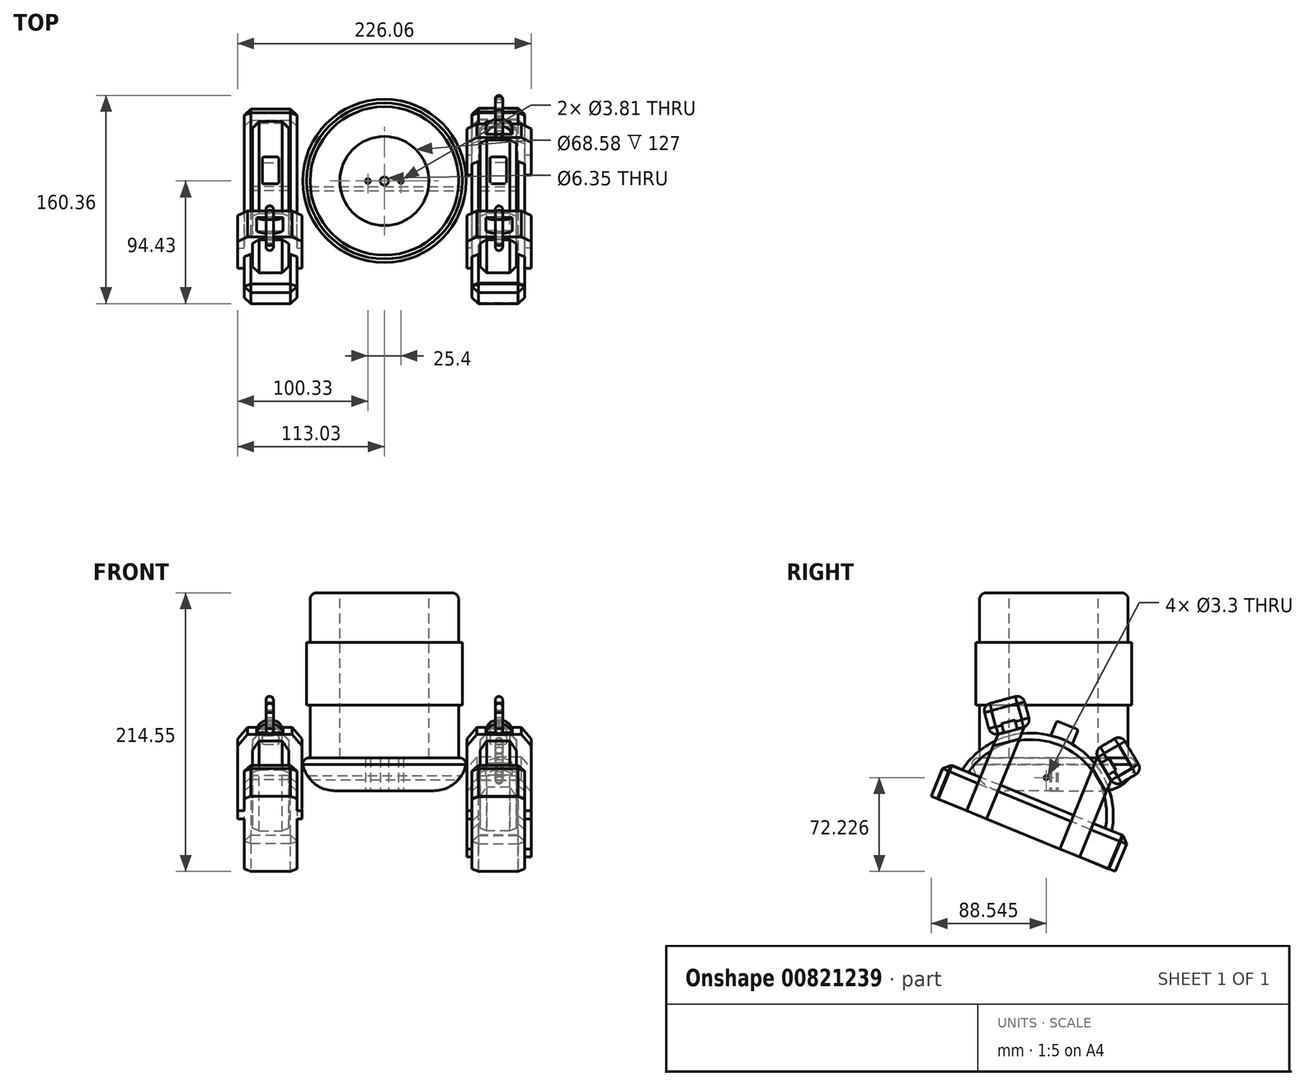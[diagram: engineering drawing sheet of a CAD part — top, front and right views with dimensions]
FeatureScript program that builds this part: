
annotation { "Feature Type Name" : "Feature", "Feature Type Description" : "" }
export const myFeature = defineFeature(function(context is Context, id is Id, definition is map)
    precondition{}
    {
        {
            assignVariable(context, id + "F0", {"name" : "Length", "anyValue" : 127 * mm});
        }
        {
            var Q0;
            Q0=qCreatedBy(makeId("Top.planeOp"),FACE);
            var sketch = newSketch(context, id + "F1", { "sketchPlane" : qUnion([Q0])});
            skCircle(sketch, "E0", {"center": v(0, 0) * mm, "radius": 57.15 * mm});
            skSolve(sketch);
        }
        {
            var Q0;
            Q0 = qSketchRegion(id + "F1", true);
            extrude(context, id + "F2", {"entities" : qUnion([Q0]), "depth" : getVariable(context, 'Length'), "offsetDistance" : 25.4 * mm});
        }
        {
            var Q0;
            Q0=makeQuery(id+"F2.opExtrude","CAP_FACE",FACE,{"disambiguationData":[OSD([sQuery(id+"F1.wireOp",EDGE,"E0")])],"isStart":false});
            var sketch = newSketch(context, id + "F3", { "sketchPlane" : qUnion([Q0])});
            skCircle(sketch, "E1", {"center": v(0, 0) * mm, "radius": 34.3 * mm});
            skSolve(sketch);
        }
        {
            var Q0;
            Q0=makeQuery(id+"F7.boolean.opBoolean","COPY",EDGE,{"derivedFrom":makeQuery(id+"F7.opExtrude","CAP_EDGE",EDGE,{"disambiguationData":[OSD([sQuery(id+"F3.wireOp",EDGE,"E1")])],"isStart":true})});
            var Q1;
            Q1=makeQuery(id+"F2.opExtrude","CAP_EDGE",EDGE,{"disambiguationData":[OSD([sQuery(id+"F1.wireOp",EDGE,"E0")])],"isStart":false});
            fillet(context, id + "F4", {"entities" : qUnion([Q0, Q1]), "radius" : 5.08 * mm, "tangentPropagation" : true, "allowEdgeOverflow" : false});
        }
        {
            var Q0;
            Q0=qCreatedBy(makeId("Top.planeOp"),FACE);
            var sketch = newSketch(context, id + "F5", { "sketchPlane" : qUnion([Q0])});
            skCircle(sketch, "E2", {"center": v(0, 0) * mm, "radius": 60 * mm});
            skSolve(sketch);
        }
        {
            var Q0;
            Q0=makeQuery(id+"F5.imprint","IMPRINT",FACE,{"disambiguationData":[TD([[makeQuery(id+"F5.imprint","IMPRINT",EDGE,{"derivedFrom":sQuery(id+"F5.wireOp",EDGE,"E2")}),1.0]])]});
            extrude(context, id + "F6", {"entities" : qUnion([Q0]), "operationType" : NewBodyOperationType.ADD, "depth" : 88.9 * mm, "offsetDistance" : 25.4 * mm, "hasSecondDirection" : true, "secondDirectionOppositeDirection" : false, "secondDirectionDepth" : 40.64 * mm});
        }
        {
            var Q0;
            Q0=makeQuery(id+"F3.imprint","IMPRINT",FACE,{"disambiguationData":[TD([[makeQuery(id+"F3.imprint","IMPRINT",EDGE,{"derivedFrom":sQuery(id+"F3.wireOp",EDGE,"E1")}),1.0]])]});
            extrude(context, id + "F7", {"entities" : qUnion([Q0]), "operationType" : NewBodyOperationType.REMOVE, "oppositeDirection" : true, "depth" : getVariable(context, 'Length'), "offsetDistance" : 25.4 * mm});
        }
        {
            var Q0;
            Q0=qCreatedBy(makeId("Top.planeOp"),FACE);
            var sketch = newSketch(context, id + "F8", { "sketchPlane" : qUnion([Q0])});
            skCircle(sketch, "E3", {"center": v(0, 0) * mm, "radius": 62.87 * mm});
            skSolve(sketch);
        }
        {
            var Q0;
            Q0 = qSketchRegion(id + "F8", true);
            extrude(context, id + "F9", {"entities" : qUnion([Q0]), "operationType" : NewBodyOperationType.ADD, "oppositeDirection" : true, "depth" : .1 * getVariable(context, 'Length'), "offsetDistance" : 25.4 * mm});
        }
        {
            var Q0;
            Q0=makeQuery(id+"F9.opExtrude","CAP_EDGE",EDGE,{"disambiguationData":[OSD([sQuery(id+"F8.wireOp",EDGE,"E3")])],"isStart":true});
            fillet(context, id + "F10", {"entities" : qUnion([Q0]), "radius" : 5.08 * mm, "tangentPropagation" : true, "allowEdgeOverflow" : false});
        }
        {
            var Q0;
            Q0=makeQuery(id+"F9.opExtrude","CAP_FACE",FACE,{"disambiguationData":[OSD([sQuery(id+"F8.wireOp",EDGE,"E3")])],"isStart":false});
            var sketch = newSketch(context, id + "F11", { "sketchPlane" : qUnion([Q0])});
            skCircle(sketch, "E4", {"center": v(0, 0) * mm, "radius": 62.87 * mm});
            skSolve(sketch);
        }
        {
            var Q0;
            Q0 = qSketchRegion(id + "F11", true);
            extrude(context, id + "F12", {"entities" : qUnion([Q0]), "operationType" : NewBodyOperationType.ADD, "depth" : .1 * getVariable(context, 'Length'), "offsetDistance" : 25.4 * mm});
        }
        {
            var Q0;
            Q0=makeQuery(id+"F12.opExtrude","CAP_EDGE",EDGE,{"disambiguationData":[OSD([sQuery(id+"F11.wireOp",EDGE,"E4")])],"isStart":false});
            fillet(context, id + "F13", {"entities" : qUnion([Q0]), "radius" : 25.4 * mm, "tangentPropagation" : true, "allowEdgeOverflow" : false});
        }
        {
            var Q0;
            Q0=makeQuery(id+"F12.opExtrude","CAP_FACE",FACE,{"disambiguationData":[OSD([sQuery(id+"F11.wireOp",EDGE,"E4")])],"isStart":false});
            var sketch = newSketch(context, id + "F14", { "sketchPlane" : qUnion([Q0])});
            skLineSegment(sketch, "E5", {"start": v(0, 0) * mm, "end": v(-12.7, 0) * mm, "construction": true});
            skLineSegment(sketch, "E6", {"start": v(0, 0) * mm, "end": v(12.7, 0) * mm, "construction": true});
            skCircle(sketch, "E7", {"center": v(-12.7, 0) * mm, "radius": 1.9 * mm});
            skCircle(sketch, "E8", {"center": v(12.7, 0) * mm, "radius": 1.9 * mm});
            skCircle(sketch, "E9", {"center": v(0, 0) * mm, "radius": 3.18 * mm});
            skSolve(sketch);
        }
        {
            var Q0;
            Q0=makeQuery(id+"F9.boolean.opBoolean","SPLIT",FACE,{"disambiguationData":[TD([makeQuery(id+"F7.boolean.opBoolean","COPY",FACE,{"derivedFrom":makeQuery(id+"F7.opExtrude","SWEPT_FACE",FACE,{"disambiguationData":[OSD([sQuery(id+"F3.wireOp",EDGE,"E1")])]})})])],"derivedFrom":makeQuery(id+"F9.opExtrude","CAP_FACE",FACE,{"disambiguationData":[OSD([sQuery(id+"F8.wireOp",EDGE,"E3")])],"isStart":true})});
            var sketch = newSketch(context, id + "F15", { "sketchPlane" : qUnion([Q0])});
            skCircle(sketch, "E10", {"center": v(0, 0) * mm, "radius": 29.15 * mm});
            skSolve(sketch);
        }
        {
            var Q0;
            Q0=makeQuery(id+"F14.imprint","IMPRINT",FACE,{"disambiguationData":[TD([[makeQuery(id+"F14.imprint","IMPRINT",EDGE,{"derivedFrom":sQuery(id+"F14.wireOp",EDGE,"E7")}),1.0]])]});
            var Q1;
            Q1=makeQuery(id+"F14.imprint","IMPRINT",FACE,{"disambiguationData":[TD([[makeQuery(id+"F14.imprint","IMPRINT",EDGE,{"derivedFrom":sQuery(id+"F14.wireOp",EDGE,"E8")}),1.0]])]});
            var Q2;
            Q2=makeQuery(id+"F14.imprint","IMPRINT",FACE,{"disambiguationData":[TD([[makeQuery(id+"F14.imprint","IMPRINT",EDGE,{"derivedFrom":sQuery(id+"F14.wireOp",EDGE,"E9")}),1.0]])]});
            var Q3;
            Q3=sQuery(id+"F14.wireOp",EDGE,"E7");
            var Q4;
            Q4=sQuery(id+"F14.wireOp",EDGE,"E8");
            var Q5;
            Q5=sQuery(id+"F15.wireOp",EDGE,"E10");
            extrude(context, id + "F16", {"entities" : qUnion([Q0, Q1, Q2]), "operationType" : NewBodyOperationType.REMOVE, "surfaceEntities" : qUnion([Q3, Q4, Q5]), "oppositeDirection" : true, "depth" : 61.2 * mm, "offsetDistance" : 25.4 * mm});
        }
        {
            var Q0;
            Q0=qCreatedBy(makeId("Right.planeOp"),FACE);
            var sketch = newSketch(context, id + "F17", { "sketchPlane" : qUnion([Q0])});
            skLineSegment(sketch, "E11", {"start": v(0, 0) * mm, "end": v(0, -44.45) * mm, "construction": true});
            skLineSegment(sketch, "E12", {"start": v(0, -44.45) * mm, "end": v(-17.78, -44.45) * mm, "construction": true});
            skCircle(sketch, "E13", {"center": v(-17.78, -44.45) * mm, "radius": 63.5 * mm});
            skLineSegment(sketch, "E14", {"start": v(-77.05, -21.67) * mm, "end": v(40.5, -69.68) * mm});
            skSolve(sketch);
        }
        {
            var Q0;
            {var subQ0=sQuery(id+"F17.wireOp",EDGE,"E14");Q0=makeQuery(id+"F17.imprint","IMPRINT",FACE,{"disambiguationData":[TD([[makeQuery(id+"F17.imprint","IMPRINT",EDGE,{"derivedFrom":subQ0}),1.0]])]});}
            extrude(context, id + "F18", {"entities" : qUnion([Q0]), "depth" : 101.6 * mm, "offsetDistance" : 25.4 * mm, "hasSecondDirection" : true, "secondDirectionOppositeDirection" : false, "secondDirectionDepth" : 73.66 * mm});
        }
        {
            var Q0;
            Q0=makeQuery(id+"F18.opExtrude","CAP_EDGE",EDGE,{"disambiguationData":[OSD([sQuery(id+"F17.wireOp",EDGE,"E13")])],"isStart":true});
            cPoint(context, id + "F19", {"entities" : qUnion([Q0]), "parameter" : 0.5});
        }
        {
            var Q0;
            Q0=makeQuery(id+"F18.opExtrude","CAP_EDGE",EDGE,{"disambiguationData":[OSD([sQuery(id+"F17.wireOp",EDGE,"E13")])],"isStart":false});
            var Q1;
            Q1 = qCreatedBy(id + "F19" ,VERTEX);
            cPlane(context, id + "F20", {"entities" : qUnion([Q0, Q1]), "cplaneType" : CPlaneType.CURVE_POINT, "offset" : 25.4 * mm, "width" : 152.4 * mm, "height" : 152.4 * mm});
        }
        {
            var Q0;
            Q0=makeQuery(id+"F18.opExtrude","SWEPT_FACE",FACE,{"disambiguationData":[OSD([sQuery(id+"F17.wireOp",EDGE,"E14")])]});
            var sketch = newSketch(context, id + "F21", { "sketchPlane" : qUnion([Q0])});
            skLineSegment(sketch, "E15.bottom", {"start": v(107.95, 76.2) * mm, "end": v(67.31, 76.2) * mm});
            skLineSegment(sketch, "E15.top", {"start": v(107.95, -76.2) * mm, "end": v(67.31, -76.2) * mm});
            skLineSegment(sketch, "E15.left", {"start": v(107.95, 76.2) * mm, "end": v(107.95, -76.2) * mm});
            skLineSegment(sketch, "E15.right", {"start": v(67.31, 76.2) * mm, "end": v(67.31, -76.2) * mm});
            skPoint(sketch, "E15.middle", {"position": v(87.63, 0) * mm});
            skPoint(sketch, "E15.middle.positionSnap0", {"position": v(87.63, 63.14) * mm});
            skPoint(sketch, "E15.centerSnap0", {"position": v(87.63, 63.14) * mm});
            skSolve(sketch);
        }
        {
            var Q0;
            Q0=makeQuery(id+"F21.imprint","IMPRINT",FACE,{"disambiguationData":[TD([[makeQuery(id+"F21.imprint","IMPRINT",EDGE,{"derivedFrom":sQuery(id+"F21.wireOp",EDGE,"E15.bottom")}),1.0]])]});
            var Q1;
            {var subQ0=sQuery(id+"F17.wireOp",EDGE,"E14");Q1=makeQuery(id+"F21.imprint","IMPRINT",FACE,{"disambiguationData":[TD([[makeQuery(id+"F21.imprint","IMPRINT",EDGE,{"derivedFrom":makeQuery(id+"F18.opExtrude","CAP_EDGE",EDGE,{"disambiguationData":[OSD([subQ0])],"isStart":true})}),1.0]])]});}
            extrude(context, id + "F22", {"entities" : qUnion([Q0, Q1]), "operationType" : NewBodyOperationType.ADD, "depth" : 13.97 * mm, "offsetDistance" : 25.4 * mm, "hasSecondDirection" : true, "secondDirectionOppositeDirection" : true, "secondDirectionDepth" : 13.97 * mm});
        }
        {
            var Q0;
            Q0=makeQuery(id+"F22.opExtrude","CAP_EDGE",EDGE,{"disambiguationData":[OSD([sQuery(id+"F21.wireOp",EDGE,"E15.bottom")])],"isStart":true});
            var Q1;
            Q1=makeQuery(id+"F22.opExtrude","CAP_EDGE",EDGE,{"disambiguationData":[OSD([sQuery(id+"F21.wireOp",EDGE,"E15.left")])],"isStart":true});
            var Q2;
            Q2=makeQuery(id+"F22.opExtrude","CAP_EDGE",EDGE,{"disambiguationData":[OSD([sQuery(id+"F21.wireOp",EDGE,"E15.right")])],"isStart":true});
            var Q3;
            Q3=makeQuery(id+"F22.opExtrude","SWEPT_EDGE",EDGE,{"disambiguationData":[OSD([sQuery(id+"F21.wireOp",EDGE,"E15.bottom"),sQuery(id+"F21.wireOp",EDGE,"E15.left")])]});
            var Q4;
            Q4=makeQuery(id+"F22.opExtrude","SWEPT_EDGE",EDGE,{"disambiguationData":[OSD([sQuery(id+"F21.wireOp",EDGE,"E15.bottom"),sQuery(id+"F21.wireOp",EDGE,"E15.right")])]});
            var Q5;
            Q5=makeQuery(id+"F22.opExtrude","SWEPT_EDGE",EDGE,{"disambiguationData":[OSD([sQuery(id+"F21.wireOp",EDGE,"E15.top"),sQuery(id+"F21.wireOp",EDGE,"E15.left")])]});
            var Q6;
            Q6=makeQuery(id+"F22.opExtrude","SWEPT_EDGE",EDGE,{"disambiguationData":[OSD([sQuery(id+"F21.wireOp",EDGE,"E15.top"),sQuery(id+"F21.wireOp",EDGE,"E15.right")])]});
            var Q7;
            Q7=makeQuery(id+"F22.opExtrude","CAP_EDGE",EDGE,{"disambiguationData":[OSD([sQuery(id+"F21.wireOp",EDGE,"E15.top")])],"isStart":true});
            var Q8;
            {var subQ0=sQuery(id+"F17.wireOp",EDGE,"E13");Q8=makeQuery(id+"F22.boolean.opBoolean","SPLIT",EDGE,{"disambiguationData":[topologyDisambiguationEdgeConnected([makeQuery(id+"F18.opExtrude","SWEPT_FACE",FACE,{"disambiguationData":[OSD([subQ0])]}),makeQuery(id+"F18.opExtrude","CAP_FACE",FACE,{"disambiguationData":[OSD([subQ0,sQuery(id+"F17.wireOp",EDGE,"E14")])],"isStart":false})])],"derivedFrom":makeQuery(id+"F18.opExtrude","CAP_EDGE",EDGE,{"disambiguationData":[OSD([subQ0])],"isStart":false})});}
            var Q9;
            {var subQ0=sQuery(id+"F17.wireOp",EDGE,"E13");Q9=makeQuery(id+"F22.boolean.opBoolean","SPLIT",EDGE,{"disambiguationData":[topologyDisambiguationEdgeConnected([makeQuery(id+"F18.opExtrude","SWEPT_FACE",FACE,{"disambiguationData":[OSD([subQ0])]}),makeQuery(id+"F18.opExtrude","CAP_FACE",FACE,{"disambiguationData":[OSD([subQ0,sQuery(id+"F17.wireOp",EDGE,"E14")])],"isStart":true})])],"derivedFrom":makeQuery(id+"F18.opExtrude","CAP_EDGE",EDGE,{"disambiguationData":[OSD([subQ0])],"isStart":true})});}
            chamfer(context, id + "F23", {"entities" : qUnion([Q0, Q1, Q2, Q3, Q4, Q5, Q6, Q7, Q8, Q9]), "width" : 5.08 * mm, "tangentPropagation" : true});
        }
        {
            var Q0;
            Q0=makeQuery(id+"F22.opExtrude","SWEPT_FACE",FACE,{"disambiguationData":[OSD([sQuery(id+"F21.wireOp",EDGE,"E15.left")])]});
            var sketch = newSketch(context, id + "F24", { "sketchPlane" : qUnion([Q0])});
            skLineSegment(sketch, "E16", {"start": v(-51.76, -47.1) * mm, "end": v(-67.05, -40.85) * mm});
            skLineSegment(sketch, "E17", {"start": v(-67.05, -40.85) * mm, "end": v(-43.04, 17.94) * mm});
            skLineSegment(sketch, "E18", {"start": v(-51.76, -47.1) * mm, "end": v(-22.95, 23.45) * mm});
            skLineSegment(sketch, "E19", {"start": v(-22.95, 23.45) * mm, "end": v(-43.04, 17.94) * mm});
            skSolve(sketch);
        }
        {
            var Q0;
            Q0 = qSketchRegion(id + "F24", true);
            extrude(context, id + "F25", {"entities" : qUnion([Q0]), "operationType" : NewBodyOperationType.ADD, "depth" : 5.08 * mm, "offsetDistance" : 25.4 * mm, "hasSecondDirection" : true, "secondDirectionOppositeDirection" : true, "secondDirectionDepth" : 44.45 * mm});
        }
        {
            var Q0;
            Q0=makeQuery(id+"F25.opExtrude","CAP_EDGE",EDGE,{"disambiguationData":[OSD([sQuery(id+"F24.wireOp",EDGE,"E19")])],"isStart":false});
            var Q1;
            Q1=makeQuery(id+"F25.opExtrude","CAP_EDGE",EDGE,{"disambiguationData":[OSD([sQuery(id+"F24.wireOp",EDGE,"E19")])],"isStart":true});
            chamfer(context, id + "F26", {"entities" : qUnion([Q0, Q1]), "width" : 7.62 * mm, "tangentPropagation" : true});
        }
        {
            var Q0;
            Q0=makeQuery(id+"F25.opExtrude","SWEPT_FACE",FACE,{"disambiguationData":[OSD([sQuery(id+"F24.wireOp",EDGE,"E19")])]});
            var sketch = newSketch(context, id + "F27", { "sketchPlane" : qUnion([Q0])});
            skSolve(sketch);
        }
        {
            var Q0;
            Q0=makeQuery(id+"F25.opExtrude","SWEPT_EDGE",EDGE,{"disambiguationData":[OSD([sQuery(id+"F24.wireOp",EDGE,"E17"),sQuery(id+"F24.wireOp",EDGE,"E19")])]});
            var Q1;
            {var subQ0=sQuery(id+"F24.wireOp",EDGE,"E19");Q1=makeQuery(id+"F27.imprint","IMPRINT",FACE,{"disambiguationData":[TD([[makeQuery(id+"F27.imprint","IMPRINT",EDGE,{"derivedFrom":makeQuery(id+"F25.opExtrude","SWEPT_EDGE",EDGE,{"disambiguationData":[OSD([sQuery(id+"F24.wireOp",EDGE,"E17"),subQ0])]})}),-1.0]])]});}
            cPlane(context, id + "F28", {"entities" : qUnion([Q0, Q1]), "cplaneType" : CPlaneType.LINE_ANGLE, "offset" : 25.4 * mm, "angle" : 90 * degree, "width" : 152.4 * mm, "height" : 152.4 * mm});
        }
        {
            var Q0;
            Q0=qCreatedBy(id+"F28.planeOp",FACE);
            cPlane(context, id + "F29", {"entities" : qUnion([Q0]), "cplaneType" : CPlaneType.OFFSET, "offset" : 10.16 * mm, "oppositeDirection" : true, "width" : 152.4 * mm, "height" : 152.4 * mm});
        }
        {
            var Q0;
            Q0=qCreatedBy(id+"F29.planeOp",FACE);
            var sketch = newSketch(context, id + "F30", { "sketchPlane" : qUnion([Q0])});
            skLineSegment(sketch, "E20.0", {"start": v(105.41, 28.7) * mm, "end": v(71.12, 28.7) * mm});
            skLineSegment(sketch, "E21", {"start": v(88.27, 28.7) * mm, "end": v(78.1, 28.7) * mm, "construction": true});
            skLineSegment(sketch, "E22", {"start": v(88.27, 28.7) * mm, "end": v(98.43, 28.7) * mm, "construction": true});
            skArc(sketch, "E23", {"start": v(98.43, 28.7) * mm, "mid": v(88.27, 36.1) * mm, "end": v(78.1, 28.7) * mm});
            skSolve(sketch);
        }
        {
            var Q0;
            {var subQ0=sQuery(id+"F30.wireOp",EDGE,"QxzVC4zv-XdtB-4Cwo-EmCr-iOd0bYjNNult");var subQ1=sQuery(id+"F30.wireOp",EDGE,"E20.0");var subQ2=makeQuery(id+"F30.imprint","INTERSECT",VERTEX,{"disambiguationData":[OD(0.0)],"derivedFrom":[subQ1,subQ0]});Q0=makeQuery(id+"F30.imprint","IMPRINT",FACE,{"disambiguationData":[TD([[makeQuery(id+"F30.imprint","IMPRINT",EDGE,{"disambiguationData":[TD([[subQ2,1.0]])],"derivedFrom":subQ1}),-1.0]])]});}
            var Q1;
            {var subQ0=sQuery(id+"F30.wireOp",EDGE,"E23");Q1=makeQuery(id+"F30.imprint","IMPRINT",FACE,{"disambiguationData":[TD([[makeQuery(id+"F30.imprint","IMPRINT",EDGE,{"derivedFrom":subQ0}),1.0]])]});}
            extrude(context, id + "F31", {"entities" : qUnion([Q0, Q1]), "operationType" : NewBodyOperationType.ADD, "endBound" : BoundingType.SYMMETRIC, "depth" : 10.67 * mm, "offsetDistance" : 25.4 * mm});
        }
        {
            var Q0;
            Q0=makeQuery(id+"F25.opExtrude","SWEPT_EDGE",EDGE,{"disambiguationData":[OSD([sQuery(id+"F24.wireOp",EDGE,"E17"),sQuery(id+"F24.wireOp",EDGE,"E19")])]});
            cPlane(context, id + "F32", {"entities" : qUnion([Q0]), "cplaneType" : CPlaneType.MID_PLANE, "offset" : 25.4 * mm, "width" : 152.4 * mm, "height" : 152.4 * mm});
        }
        {
            var Q0;
            Q0=qCreatedBy(id+"F32.planeOp",FACE);
            var sketch = newSketch(context, id + "F33", { "sketchPlane" : qUnion([Q0])});
            skLineSegment(sketch, "E24", {"start": v(38.39, 19.22) * mm, "end": v(40.35, 26.37) * mm});
            skLineSegment(sketch, "E25", {"start": v(30.06, 29.2) * mm, "end": v(40.35, 26.37) * mm});
            skLineSegment(sketch, "E26", {"start": v(28.1, 22.04) * mm, "end": v(30.06, 29.2) * mm});
            skLineSegment(sketch, "E27.bottom", {"start": v(28.78, 43.95) * mm, "end": v(48.41, 38.69) * mm});
            skLineSegment(sketch, "E27.top", {"start": v(24.18, 26.77) * mm, "end": v(43.81, 21.52) * mm});
            skLineSegment(sketch, "E27.left", {"start": v(25.67, 42.15) * mm, "end": v(22.39, 29.89) * mm});
            skLineSegment(sketch, "E27.right", {"start": v(50.2, 35.58) * mm, "end": v(46.92, 23.31) * mm});
            skPoint(sketch, "E27.middle", {"position": v(36.23, 31.16) * mm});
            skPoint(sketch, "E28.visualSharp", {"position": v(26.33, 44.6) * mm});
            skArc(sketch, "E28.filletArc", {"start": v(28.78, 43.95) * mm, "mid": v(26.86, 43.7) * mm, "end": v(25.67, 42.15) * mm});
            skPoint(sketch, "E29.visualSharp", {"position": v(21.73, 27.43) * mm});
            skArc(sketch, "E29.filletArc", {"start": v(22.39, 29.89) * mm, "mid": v(22.64, 27.96) * mm, "end": v(24.18, 26.77) * mm});
            skPoint(sketch, "E30.visualSharp", {"position": v(46.26, 20.86) * mm});
            skArc(sketch, "E30.filletArc", {"start": v(43.81, 21.52) * mm, "mid": v(45.74, 21.77) * mm, "end": v(46.92, 23.31) * mm});
            skPoint(sketch, "E31.visualSharp", {"position": v(50.87, 38.03) * mm});
            skArc(sketch, "E31.filletArc", {"start": v(50.2, 35.58) * mm, "mid": v(49.95, 37.5) * mm, "end": v(48.41, 38.69) * mm});
            skSolve(sketch);
        }
        {
            var Q0;
            Q0=makeQuery(id+"F31.opExtrude","CAP_FACE",FACE,{"disambiguationData":[OSD([sQuery(id+"F30.wireOp",EDGE,"E20.0"),sQuery(id+"F30.wireOp",EDGE,"E23")])],"isStart":false});
            var sketch = newSketch(context, id + "F34", { "sketchPlane" : qUnion([Q0])});
            skLineSegment(sketch, "E32", {"start": v(88.27, 36.1) * mm, "end": v(88.27, 31.83) * mm});
            skLineSegment(sketch, "E33", {"start": v(88.27, 50.1) * mm, "end": v(88.27, 36.1) * mm});
            skCircle(sketch, "E34", {"center": v(88.27, 31.83) * mm, "radius": 2.8 * mm});
            skSolve(sketch);
        }
        {
            var Q0;
            Q0=makeQuery(id+"F34.imprint","IMPRINT",FACE,{"disambiguationData":[TD([[makeQuery(id+"F34.imprint","IMPRINT",EDGE,{"derivedFrom":sQuery(id+"F34.wireOp",EDGE,"E34")}),1.0]])]});
            var Q1;
            Q1=sQuery(id+"F33.wireOp",EDGE,"E27.top");
            var Q2;
            Q2=sQuery(id+"F33.wireOp",EDGE,"E30.filletArc");
            var Q3;
            Q3=sQuery(id+"F33.wireOp",EDGE,"E27.right");
            var Q4;
            Q4=sQuery(id+"F33.wireOp",EDGE,"E31.filletArc");
            var Q5;
            Q5=sQuery(id+"F33.wireOp",EDGE,"E27.bottom");
            var Q6;
            Q6=sQuery(id+"F33.wireOp",EDGE,"E28.filletArc");
            var Q7;
            Q7=sQuery(id+"F33.wireOp",EDGE,"E27.left");
            var Q8;
            Q8=sQuery(id+"F33.wireOp",EDGE,"E29.filletArc");
            sweep(context, id + "F35", {"operationType" : NewBodyOperationType.ADD, "profiles" : qUnion([Q0]), "path" : qUnion([Q1, Q2, Q3, Q4, Q5, Q6, Q7, Q8])});
        }
        {
            var Q0;
            Q0=qCreatedBy(id+"F20.planeOp",FACE);
            var sketch = newSketch(context, id + "F36", { "sketchPlane" : qUnion([Q0])});
            skLineSegment(sketch, "E35", {"start": v(78.74, 15.63) * mm, "end": v(96.52, 15.63) * mm});
            skLineSegment(sketch, "E36.bottom", {"start": v(93.98, 27.06) * mm, "end": v(81.28, 27.06) * mm});
            skLineSegment(sketch, "E36.top", {"start": v(93.98, 4.2) * mm, "end": v(81.28, 4.2) * mm});
            skLineSegment(sketch, "E36.left", {"start": v(93.98, 27.06) * mm, "end": v(93.98, 4.2) * mm});
            skLineSegment(sketch, "E36.right", {"start": v(81.28, 27.06) * mm, "end": v(81.28, 4.2) * mm});
            skPoint(sketch, "E36.middle", {"position": v(87.63, 15.63) * mm});
            skSolve(sketch);
        }
        {
            var Q0;
            Q0 = qSketchRegion(id + "F36", true);
            extrude(context, id + "F37", {"entities" : qUnion([Q0]), "operationType" : NewBodyOperationType.ADD, "endBound" : BoundingType.SYMMETRIC, "depth" : 17.78 * mm, "offsetDistance" : 25.4 * mm});
        }
        {
            var Q0;
            Q0=makeQuery(id+"F37.opExtrude","CAP_EDGE",EDGE,{"disambiguationData":[OSD([sQuery(id+"F36.wireOp",EDGE,"E36.bottom")])],"isStart":false});
            var Q1;
            Q1=makeQuery(id+"F37.opExtrude","CAP_EDGE",EDGE,{"disambiguationData":[OSD([sQuery(id+"F36.wireOp",EDGE,"E36.bottom")])],"isStart":true});
            var Q2;
            Q2=makeQuery(id+"F37.opExtrude","CAP_EDGE",EDGE,{"disambiguationData":[OSD([sQuery(id+"F36.wireOp",EDGE,"E36.left")])],"isStart":false});
            var Q3;
            Q3=makeQuery(id+"F37.opExtrude","CAP_EDGE",EDGE,{"disambiguationData":[OSD([sQuery(id+"F36.wireOp",EDGE,"E36.left")])],"isStart":true});
            var Q4;
            Q4=makeQuery(id+"F37.opExtrude","CAP_EDGE",EDGE,{"disambiguationData":[OSD([sQuery(id+"F36.wireOp",EDGE,"E36.right")])],"isStart":true});
            var Q5;
            Q5=makeQuery(id+"F37.opExtrude","CAP_EDGE",EDGE,{"disambiguationData":[OSD([sQuery(id+"F36.wireOp",EDGE,"E36.right")])],"isStart":false});
            var Q6;
            Q6=makeQuery(id+"F37.opExtrude","SWEPT_EDGE",EDGE,{"disambiguationData":[OSD([sQuery(id+"F36.wireOp",EDGE,"E36.bottom"),sQuery(id+"F36.wireOp",EDGE,"E36.left")])]});
            var Q7;
            Q7=makeQuery(id+"F37.opExtrude","SWEPT_EDGE",EDGE,{"disambiguationData":[OSD([sQuery(id+"F36.wireOp",EDGE,"E36.bottom"),sQuery(id+"F36.wireOp",EDGE,"E36.right")])]});
            fillet(context, id + "F38", {"entities" : qUnion([Q0, Q1, Q2, Q3, Q4, Q5, Q6, Q7]), "radius" : 1.27 * mm, "tangentPropagation" : true, "allowEdgeOverflow" : false});
        }
        {
            var Q0;
            Q0=makeQuery(id+"F18.opExtrude","SWEPT_BODY",BODY,{"disambiguationData":[OSD([sQuery(id+"F17.wireOp",EDGE,"E13"),sQuery(id+"F17.wireOp",EDGE,"E14")])]});
            var Q1;
            Q1=qCreatedBy(id+"F20.planeOp",FACE);
            mirror(context, id + "F39", {"operationType" : NewBodyOperationType.ADD, "entities" : qUnion([Q0]), "mirrorPlane" : qUnion([Q1])});
        }
        {
            var Q0;
            {var subQ1=makeQuery(id+"F25.opExtrude","SWEPT_FACE",FACE,{"disambiguationData":[OSD([sQuery(id+"F24.wireOp",EDGE,"E18")])]});var subQ2=sQuery(id+"F17.wireOp",EDGE,"E13");Q0=makeQuery(id+"F39.boolean.opBoolean","SPLIT",FACE,{"disambiguationData":[TD([subQ1])],"derivedFrom":makeQuery(id+"F25.boolean.opBoolean","SPLIT",FACE,{"disambiguationData":[TD([subQ1])],"derivedFrom":makeQuery(id+"F18.opExtrude","CAP_FACE",FACE,{"disambiguationData":[OSD([subQ2,sQuery(id+"F17.wireOp",EDGE,"E14")])],"isStart":false})})});}
            var sketch = newSketch(context, id + "F40", { "sketchPlane" : qUnion([Q0])});
            skLineSegment(sketch, "E37", {"start": v(-5.32, -13.93) * mm, "end": v(-13, -32.74) * mm, "construction": true});
            skLineSegment(sketch, "E38", {"start": v(-5.32, -13.93) * mm, "end": v(-6.45, -16.72) * mm, "construction": true});
            skCircle(sketch, "E39", {"center": v(-5.89, -15.32) * mm, "radius": 1.65 * mm});
            skSolve(sketch);
        }
        {
            var Q0;
            Q0=makeQuery(id+"F40.imprint","IMPRINT",FACE,{"disambiguationData":[TD([[makeQuery(id+"F40.imprint","IMPRINT",EDGE,{"derivedFrom":sQuery(id+"F40.wireOp",EDGE,"E39")}),1.0]])]});
            extrude(context, id + "F41", {"entities" : qUnion([Q0]), "operationType" : NewBodyOperationType.REMOVE, "oppositeDirection" : true, "depth" : 271.53 * mm, "offsetDistance" : 25.4 * mm});
        }
        {
            var Q0;
            Q0=qCreatedBy(makeId("Right.planeOp"),FACE);
            var sketch = newSketch(context, id + "F42", { "sketchPlane" : qUnion([Q0])});
            skCircle(sketch, "E40.0", {"center": v(-5.89, -15.32) * mm, "radius": 1.65 * mm});
            skSolve(sketch);
        }
        {
            var Q0;
            Q0=makeQuery(id+"F18.opExtrude","SWEPT_BODY",BODY,{"disambiguationData":[OSD([sQuery(id+"F17.wireOp",EDGE,"aac23f5f-ffa8-4f8b-bb25-5ba39ca1218b.0"),sQuery(id+"F17.wireOp",EDGE,"E13"),sQuery(id+"F17.wireOp",EDGE,"E14")])]});
            var Q1;
            Q1=qCreatedBy(makeId("Right.planeOp"),FACE);
            mirror(context, id + "F43", {"entities" : qUnion([Q0]), "mirrorPlane" : qUnion([Q1])});
        }
        {
            var Q0;
            Q0 = qSketchRegion(id + "F42", true);
            extrude(context, id + "F44", {"entities" : qUnion([Q0]), "operationType" : NewBodyOperationType.REMOVE, "oppositeDirection" : true, "depth" : 106.17 * mm, "offsetDistance" : 25.4 * mm, "hasSecondDirection" : true, "secondDirectionOppositeDirection" : false, "secondDirectionDepth" : 98.8 * mm});
        }
    });
